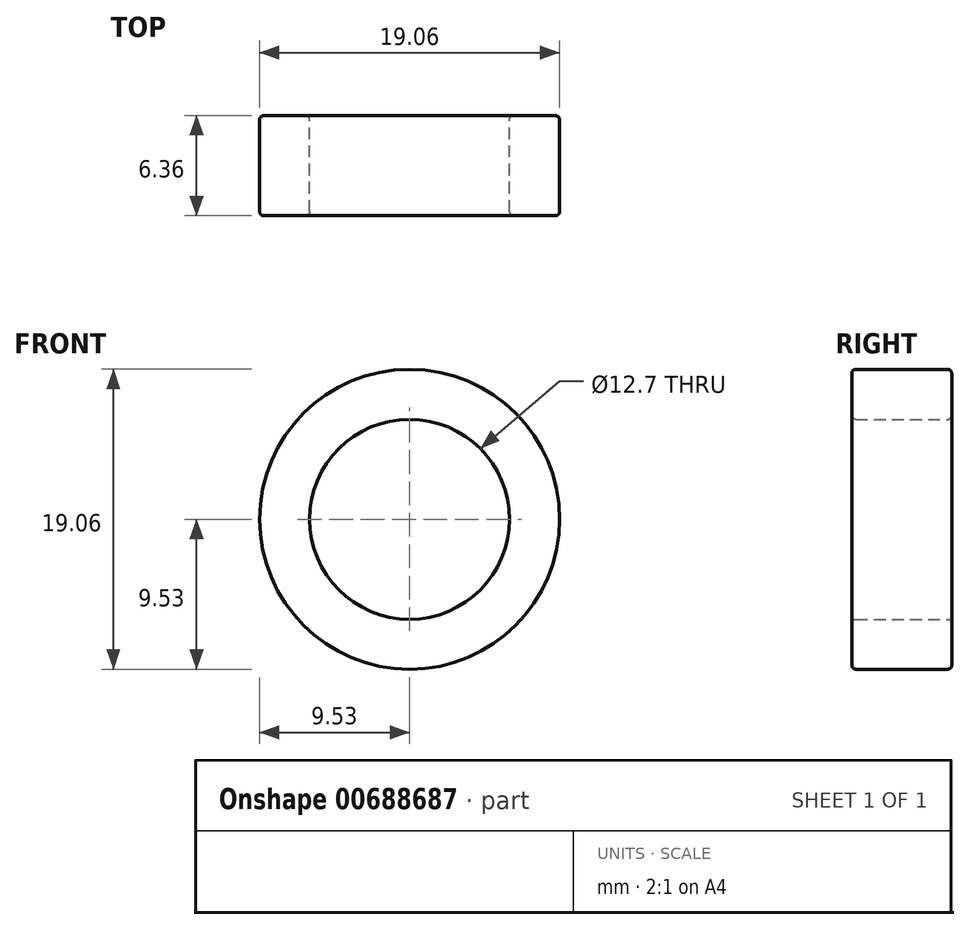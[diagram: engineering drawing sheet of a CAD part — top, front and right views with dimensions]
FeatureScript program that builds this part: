
annotation { "Feature Type Name" : "Feature", "Feature Type Description" : "" }
export const myFeature = defineFeature(function(context is Context, id is Id, definition is map)
    precondition{}
    {
        {
            var Q0;
            Q0=qCreatedBy(makeId("Front.planeOp"),FACE);
            var sketch = newSketch(context, id + "F0", { "sketchPlane" : qUnion([Q0])});
            skCircle(sketch, "E0", {"center": v(0, 0) * mm, "radius": 9.53 * mm});
            skCircle(sketch, "E1", {"center": v(0, 0) * mm, "radius": 6.35 * mm});
            skSolve(sketch);
        }
        {
            var Q0;
            Q0 = qSketchRegion(id + "F0", true);
            extrude(context, id + "F1", {"entities" : qUnion([Q0]), "endBound" : BoundingType.SYMMETRIC, "depth" : 6.35 * mm, "offsetDistance" : 25.4 * mm});
        }
        {
            var Q0;
            Q0=makeQuery(id+"F1.opExtrude","CAP_EDGE",EDGE,{"disambiguationData":[OSD([sQuery(id+"F0.wireOp",EDGE,"E0")])],"isStart":true});
            var Q1;
            Q1=makeQuery(id+"F1.opExtrude","CAP_EDGE",EDGE,{"disambiguationData":[OSD([sQuery(id+"F0.wireOp",EDGE,"E0")])],"isStart":false});
            var Q2;
            Q2=makeQuery(id+"F1.opExtrude","CAP_EDGE",EDGE,{"disambiguationData":[OSD([sQuery(id+"F0.wireOp",EDGE,"E1")])],"isStart":true});
            var Q3;
            Q3=makeQuery(id+"F1.opExtrude","CAP_EDGE",EDGE,{"disambiguationData":[OSD([sQuery(id+"F0.wireOp",EDGE,"E1")])],"isStart":false});
            fillet(context, id + "F2", {"entities" : qUnion([Q0, Q1, Q2, Q3]), "radius" : 0.25 * mm, "tangentPropagation" : true, "allowEdgeOverflow" : false});
        }
    });
